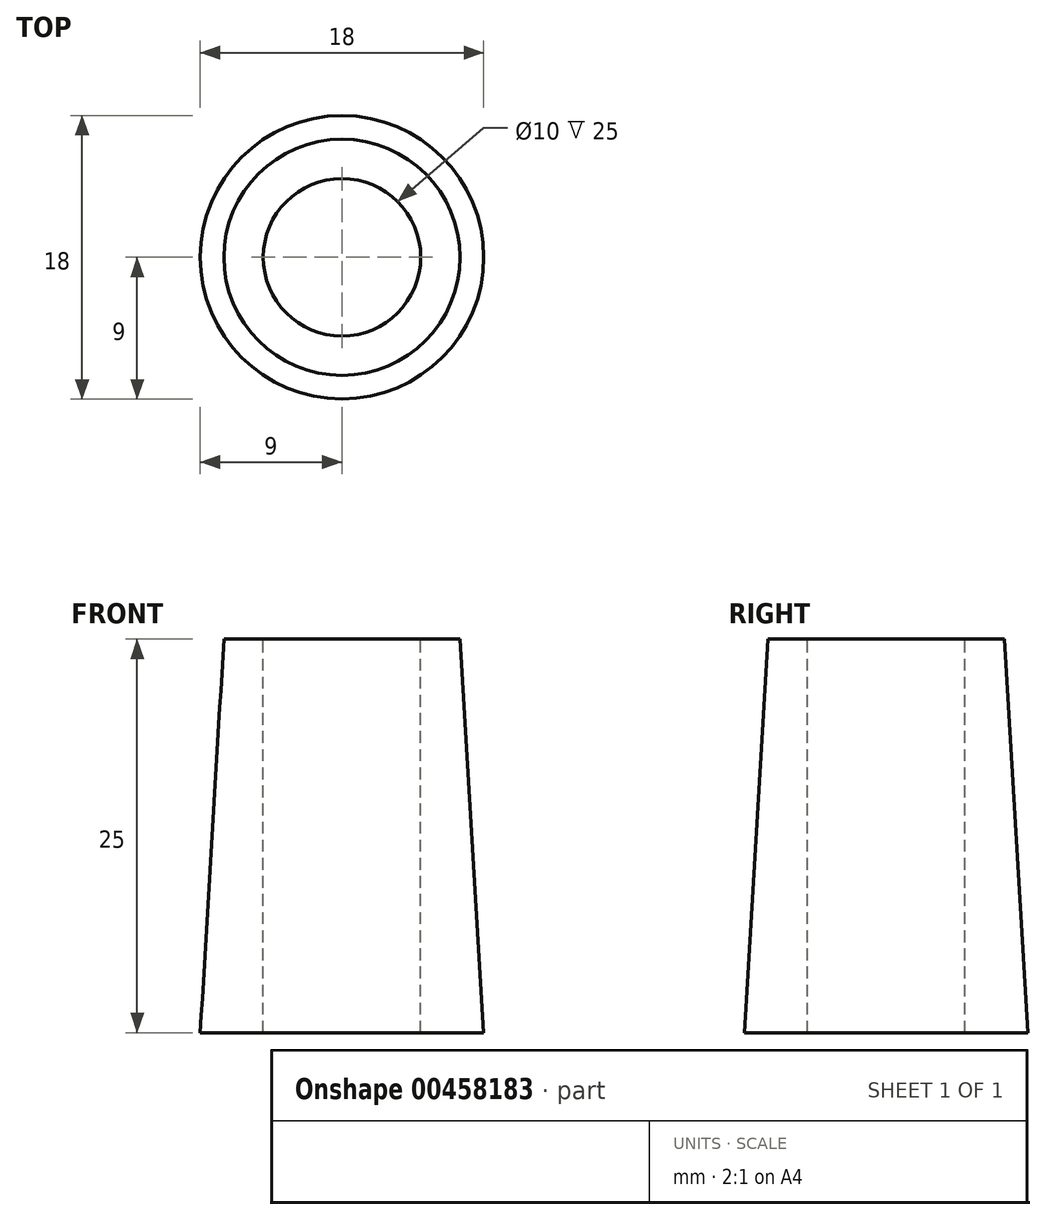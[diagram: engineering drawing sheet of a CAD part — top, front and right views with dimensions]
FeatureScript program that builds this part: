
annotation { "Feature Type Name" : "Feature", "Feature Type Description" : "" }
export const myFeature = defineFeature(function(context is Context, id is Id, definition is map)
    precondition{}
    {
        {
            var Q0;
            Q0=qCreatedBy(makeId("Top.planeOp"),FACE);
            var sketch = newSketch(context, id + "F0", { "sketchPlane" : qUnion([Q0])});
            skCircle(sketch, "E0", {"center": v(0, 0) * mm, "radius": 9 * mm});
            skCircle(sketch, "E1", {"center": v(0, 0) * mm, "radius": 5 * mm});
            skPoint(sketch, "E2", {"position": v(0, -9) * mm});
            skSolve(sketch);
        }
        {
            var Q0;
            Q0=qCreatedBy(makeId("Top.planeOp"),FACE);
            cPlane(context, id + "F1", {"entities" : qUnion([Q0]), "cplaneType" : CPlaneType.OFFSET, "offset" : 25 * mm, "width" : 150 * mm, "height" : 150 * mm});
        }
        {
            var Q0;
            Q0=qCreatedBy(id+"F1.planeOp",FACE);
            var sketch = newSketch(context, id + "F2", { "sketchPlane" : qUnion([Q0])});
            skCircle(sketch, "E3", {"center": v(0, 0) * mm, "radius": 7.5 * mm});
            skCircle(sketch, "E4", {"center": v(0, 0) * mm, "radius": 5 * mm});
            skPoint(sketch, "E5", {"position": v(0, -7.5) * mm});
            skSolve(sketch);
        }
        {
            var Q0;
            Q0=makeQuery(id+"F2.imprint","IMPRINT",FACE,{"disambiguationData":[TD([[makeQuery(id+"F2.imprint","IMPRINT",EDGE,{"derivedFrom":sQuery(id+"F2.wireOp",EDGE,"E3")}),1.0]])]});
            extrude(context, id + "F3", {"entities" : qUnion([Q0]), "oppositeDirection" : true, "depth" : 25 * mm, "offsetDistance" : 25 * mm});
        }
        {
            var Q0;
            Q0=qCreatedBy(makeId("Right.planeOp"),FACE);
            var sketch = newSketch(context, id + "F4", { "sketchPlane" : qUnion([Q0])});
            skLineSegment(sketch, "E6", {"start": v(-9, 0) * mm, "end": v(-7.5, 25) * mm});
            skLineSegment(sketch, "E7", {"start": v(-9, 0) * mm, "end": v(-7.5, 0) * mm});
            skLineSegment(sketch, "E8", {"start": v(-7.5, 0) * mm, "end": v(-7.5, 25) * mm});
            skSolve(sketch);
        }
        {
            var Q0;
            Q0=makeQuery(id+"F4.imprint","IMPRINT",FACE,{"disambiguationData":[TD([[makeQuery(id+"F4.imprint","IMPRINT",EDGE,{"derivedFrom":sQuery(id+"F4.wireOp",EDGE,"E6")}),-1.0]])]});
            var Q1;
            Q1=sQuery(id+"F0.wireOp",EDGE,"E0");
            revolve(context, id + "F5", {"operationType" : NewBodyOperationType.ADD, "entities" : qUnion([Q0]), "axis" : qUnion([Q1]), "revolveType" : RevolveType.FULL});
        }
    });
